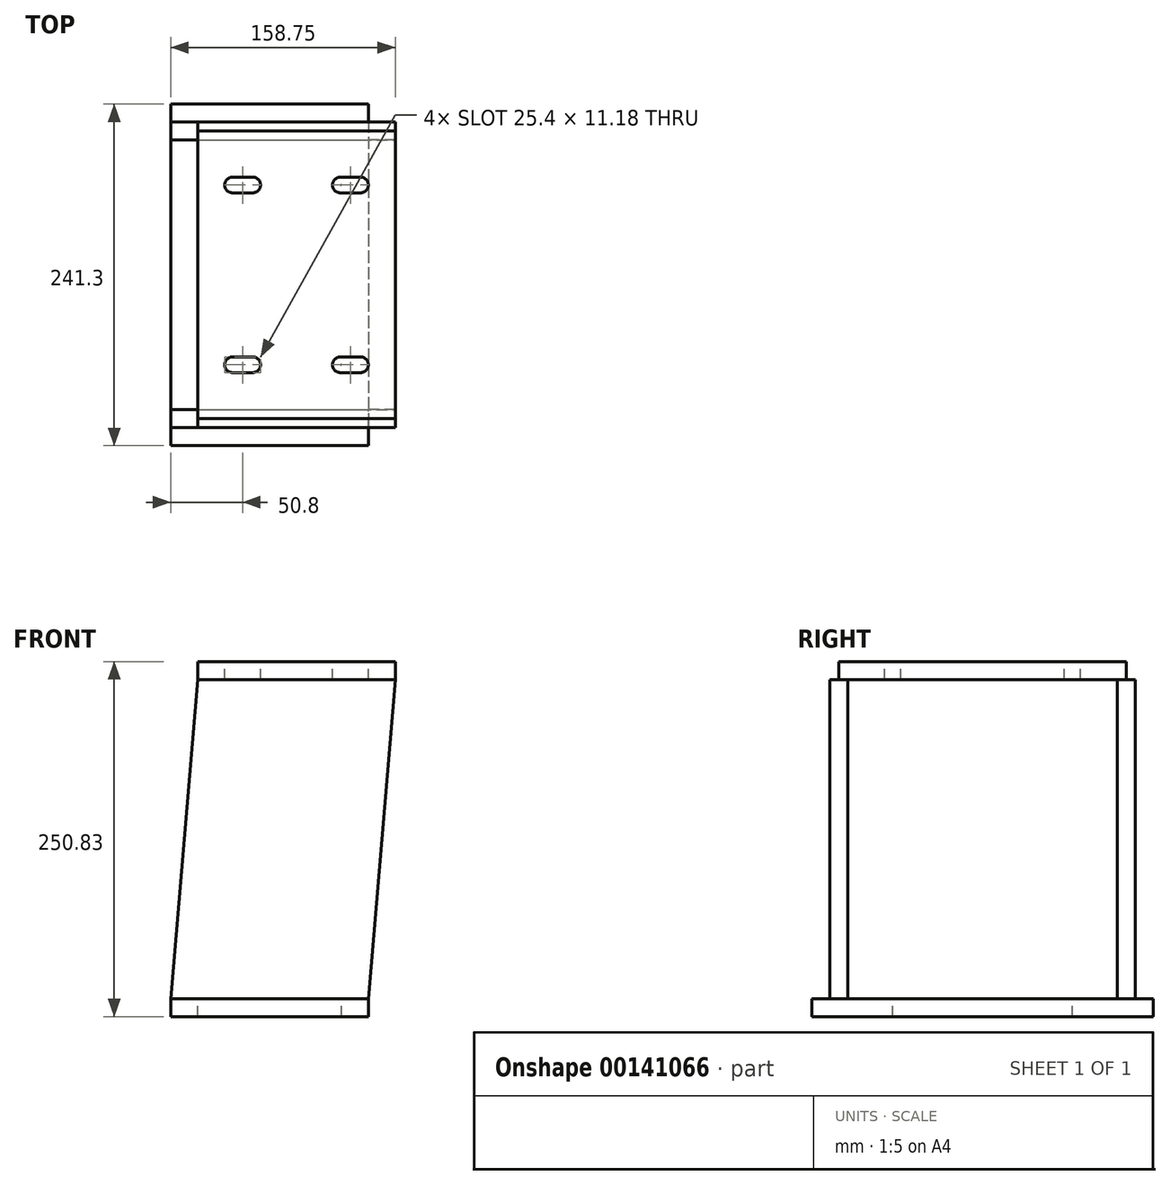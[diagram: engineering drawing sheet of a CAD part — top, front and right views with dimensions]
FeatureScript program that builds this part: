
annotation { "Feature Type Name" : "Feature", "Feature Type Description" : "" }
export const myFeature = defineFeature(function(context is Context, id is Id, definition is map)
    precondition{}
    {
        {
            var Q0;
            Q0=qCreatedBy(makeId("Top.planeOp"),FACE);
            cPlane(context, id + "F0", {"entities" : qUnion([Q0]), "cplaneType" : CPlaneType.OFFSET, "offset" : 250.82 * mm, "width" : 152.4 * mm, "height" : 152.4 * mm});
        }
        {
            var Q0;
            Q0=qCreatedBy(makeId("Top.planeOp"),FACE);
            var sketch = newSketch(context, id + "F1", { "sketchPlane" : qUnion([Q0])});
            skLineSegment(sketch, "E0.bottom", {"start": v(-69.85, 120.65) * mm, "end": v(69.85, 120.65) * mm});
            skLineSegment(sketch, "E0.top", {"start": v(-69.85, -120.65) * mm, "end": v(69.85, -120.65) * mm});
            skLineSegment(sketch, "E0.left", {"start": v(-69.85, 120.65) * mm, "end": v(-69.85, -120.65) * mm});
            skLineSegment(sketch, "E0.right", {"start": v(69.85, 120.65) * mm, "end": v(69.85, -120.65) * mm});
            skPoint(sketch, "E0.middle", {"position": v(0, 0) * mm});
            skSolve(sketch);
        }
        {
            var Q0;
            Q0 = qSketchRegion(id + "F1", true);
            extrude(context, id + "F2", {"entities" : qUnion([Q0]), "depth" : 12.7 * mm});
        }
        {
            var Q0;
            Q0=makeQuery(id+"F2.opExtrude","CAP_FACE",FACE,{"disambiguationData":[OSD([sQuery(id+"F1.wireOp",EDGE,"E0.bottom"),sQuery(id+"F1.wireOp",EDGE,"E0.top"),sQuery(id+"F1.wireOp",EDGE,"E0.left"),sQuery(id+"F1.wireOp",EDGE,"E0.right")])],"isStart":false});
            var sketch = newSketch(context, id + "F3", { "sketchPlane" : qUnion([Q0])});
            skLineSegment(sketch, "E1.0", {"start": v(69.85, 120.65) * mm, "end": v(69.85, -120.65) * mm, "construction": true});
            skLineSegment(sketch, "E2.0", {"start": v(50.8, 120.65) * mm, "end": v(50.8, -120.65) * mm, "construction": true});
            skLineSegment(sketch, "E3.0", {"start": v(-50.8, 120.65) * mm, "end": v(-50.8, -120.65) * mm, "construction": true});
            skLineSegment(sketch, "E4", {"start": v(-147.29, 0) * mm, "end": v(150.02, 0) * mm, "construction": true});
            skLineSegment(sketch, "E5.0", {"start": v(-147.29, -63.5) * mm, "end": v(150.02, -63.5) * mm, "construction": true});
            skLineSegment(sketch, "E6.MirrorCS", {"start": v(-147.29, 63.5) * mm, "end": v(150.02, 63.5) * mm, "construction": true});
            skPoint(sketch, "E7", {"position": v(-50.8, 63.5) * mm});
            skPoint(sketch, "E8", {"position": v(50.8, 63.5) * mm});
            skPoint(sketch, "E9", {"position": v(50.8, -63.5) * mm});
            skPoint(sketch, "E10", {"position": v(-50.8, -63.5) * mm});
            skSolve(sketch);
        }
        {
            var Q0;
            Q0=sQuery(id+"F3.wireOp",VERTEX,"E7");
            var Q1;
            Q1=sQuery(id+"F3.wireOp",VERTEX,"E8");
            var Q2;
            Q2=sQuery(id+"F3.wireOp",VERTEX,"E9");
            var Q3;
            Q3=sQuery(id+"F3.wireOp",VERTEX,"E10");
            var Q4;
            Q4=makeQuery(id+"F2.opExtrude","SWEPT_BODY",BODY,{"disambiguationData":[OSD([sQuery(id+"F1.wireOp",EDGE,"E0.bottom"),sQuery(id+"F1.wireOp",EDGE,"E0.top"),sQuery(id+"F1.wireOp",EDGE,"E0.left"),sQuery(id+"F1.wireOp",EDGE,"E0.right")])]});
            hole(context, id + "F4", {"style" : HoleStyle.SIMPLE, "endStyle" : HoleEndStyle.THROUGH, "standardTappedOrClearance" : lookupTablePath({ "standard" : "ANSI", "size" : "9/16 (0.56)", "type" : "Drilled" }), "standardBlindInLast" : lookupTablePath({ "standard" : "ANSI", "size" : "9/16", "type" : "Drilled" }), "holeDiameter" : 9 / 406.4 * mm, "locations" : qUnion([Q0, Q1, Q2, Q3]), "scope" : qUnion([Q4]), "isTappedThrough" : true});
        }
        {
            var Q0;
            Q0=qCreatedBy(id+"F0.planeOp",FACE);
            var sketch = newSketch(context, id + "F5", { "sketchPlane" : qUnion([Q0])});
            skLineSegment(sketch, "E11", {"start": v(0, 141.47) * mm, "end": v(0, -163.23) * mm, "construction": true});
            skLineSegment(sketch, "E12", {"start": v(-208.48, 0) * mm, "end": v(177.55, 0) * mm, "construction": true});
            skLineSegment(sketch, "E13.0", {"start": v(19.05, 141.47) * mm, "end": v(19.05, -163.23) * mm, "construction": true});
            skLineSegment(sketch, "E14.bottom", {"start": v(-50.8, 101.6) * mm, "end": v(88.9, 101.6) * mm});
            skLineSegment(sketch, "E14.top", {"start": v(-50.8, -101.6) * mm, "end": v(88.9, -101.6) * mm});
            skLineSegment(sketch, "E14.left", {"start": v(-50.8, 101.6) * mm, "end": v(-50.8, -101.6) * mm});
            skLineSegment(sketch, "E14.right", {"start": v(88.9, 101.6) * mm, "end": v(88.9, -101.6) * mm});
            skPoint(sketch, "E14.middle", {"position": v(19.05, 0) * mm});
            skSolve(sketch);
        }
        {
            var Q0;
            Q0 = qSketchRegion(id + "F5", true);
            extrude(context, id + "F6", {"entities" : qUnion([Q0]), "oppositeDirection" : true, "depth" : 12.7 * mm});
        }
        {
            var Q0;
            Q0=makeQuery(id+"F6.opExtrude","CAP_FACE",FACE,{"disambiguationData":[OSD([sQuery(id+"F5.wireOp",EDGE,"E14.bottom"),sQuery(id+"F5.wireOp",EDGE,"E14.top"),sQuery(id+"F5.wireOp",EDGE,"E14.left"),sQuery(id+"F5.wireOp",EDGE,"E14.right")])],"isStart":true});
            var sketch = newSketch(context, id + "F7", { "sketchPlane" : qUnion([Q0])});
            skLineSegment(sketch, "E15", {"start": v(-136.74, 0) * mm, "end": v(178.27, 0) * mm, "construction": true});
            skPoint(sketch, "E15.endSnap0", {"position": v(-50.8, 0) * mm});
            skLineSegment(sketch, "E16", {"start": v(19.05, 101.6) * mm, "end": v(19.05, -101.6) * mm, "construction": true});
            skLineSegment(sketch, "E17.0", {"start": v(-19.05, 101.6) * mm, "end": v(-19.05, -101.6) * mm, "construction": true});
            skLineSegment(sketch, "E18.0", {"start": v(-136.74, -63.5) * mm, "end": v(-26.16, -63.5) * mm, "construction": true});
            skLineSegment(sketch, "E19.0", {"start": v(-26.16, 101.6) * mm, "end": v(-26.16, -101.6) * mm, "construction": true});
            skLineSegment(sketch, "E20.MirrorCS", {"start": v(-11.94, 101.6) * mm, "end": v(-11.94, -101.6) * mm, "construction": true});
            skLineSegment(sketch, "E21.trimOffspring", {"start": v(-11.94, -63.5) * mm, "end": v(178.27, -63.5) * mm, "construction": true});
            skLineSegment(sketch, "E22", {"start": v(-26.16, -63.5) * mm, "end": v(-11.94, -63.5) * mm});
            skArc(sketch, "E23.0.startCap", {"start": v(-26.16, -69.09) * mm, "mid": v(-31.75, -63.5) * mm, "end": v(-26.16, -57.91) * mm});
            skArc(sketch, "E23.0.endCap", {"start": v(-11.94, -57.91) * mm, "mid": v(-6.35, -63.5) * mm, "end": v(-11.94, -69.09) * mm});
            skLineSegment(sketch, "E23.0.left", {"start": v(-26.16, -57.91) * mm, "end": v(-11.94, -57.91) * mm});
            skLineSegment(sketch, "E23.0.right", {"start": v(-26.16, -69.09) * mm, "end": v(-11.94, -69.09) * mm});
            skLineSegment(sketch, "E24.MirrorCS", {"start": v(64.26, -69.09) * mm, "end": v(50.04, -69.09) * mm});
            skLineSegment(sketch, "E25.MirrorCS", {"start": v(64.26, -57.91) * mm, "end": v(50.04, -57.91) * mm});
            skArc(sketch, "E26.MirrorCS", {"start": v(50.04, -57.91) * mm, "mid": v(44.45, -63.5) * mm, "end": v(50.04, -69.09) * mm});
            skArc(sketch, "E27.MirrorCS", {"start": v(64.26, -69.09) * mm, "mid": v(69.85, -63.5) * mm, "end": v(64.26, -57.91) * mm});
            skLineSegment(sketch, "E28.MirrorCS", {"start": v(64.26, -63.5) * mm, "end": v(50.04, -63.5) * mm});
            skLineSegment(sketch, "E29.MirrorCS", {"start": v(64.26, 69.09) * mm, "end": v(50.04, 69.09) * mm});
            skLineSegment(sketch, "E30.MirrorCS", {"start": v(-26.16, 69.09) * mm, "end": v(-11.94, 69.09) * mm});
            skLineSegment(sketch, "E31.MirrorCS", {"start": v(-26.16, 57.91) * mm, "end": v(-11.94, 57.91) * mm});
            skArc(sketch, "E32.MirrorCS", {"start": v(-11.94, 57.91) * mm, "mid": v(-6.35, 63.5) * mm, "end": v(-11.94, 69.09) * mm});
            skArc(sketch, "E33.MirrorCS", {"start": v(-26.16, 69.09) * mm, "mid": v(-31.75, 63.5) * mm, "end": v(-26.16, 57.91) * mm});
            skLineSegment(sketch, "E34.MirrorCS", {"start": v(-26.16, 63.5) * mm, "end": v(-11.94, 63.5) * mm});
            skLineSegment(sketch, "E35.MirrorCS", {"start": v(64.26, 63.5) * mm, "end": v(50.04, 63.5) * mm});
            skLineSegment(sketch, "E36.MirrorCS", {"start": v(64.26, 57.91) * mm, "end": v(50.04, 57.91) * mm});
            skArc(sketch, "E37.MirrorCS", {"start": v(50.04, 57.91) * mm, "mid": v(44.45, 63.5) * mm, "end": v(50.04, 69.09) * mm});
            skArc(sketch, "E38.MirrorCS", {"start": v(64.26, 69.09) * mm, "mid": v(69.85, 63.5) * mm, "end": v(64.26, 57.91) * mm});
            skSolve(sketch);
        }
        {
            var Q0;
            Q0 = qSketchRegion(id + "F7", true);
            extrude(context, id + "F8", {"entities" : qUnion([Q0]), "operationType" : NewBodyOperationType.REMOVE, "oppositeDirection" : true, "depth" : 25.4 * mm});
        }
        {
            var Q0;
            Q0=makeQuery(id+"F6.opExtrude","SWEPT_FACE",FACE,{"disambiguationData":[OSD([sQuery(id+"F5.wireOp",EDGE,"E14.top")])]});
            var sketch = newSketch(context, id + "F9", { "sketchPlane" : qUnion([Q0])});
            skLineSegment(sketch, "E39.0", {"start": v(-50.8, 238.13) * mm, "end": v(88.9, 238.13) * mm});
            skLineSegment(sketch, "E40.0", {"start": v(-69.85, 12.7) * mm, "end": v(69.85, 12.7) * mm});
            skLineSegment(sketch, "E41", {"start": v(-50.8, 238.13) * mm, "end": v(-69.85, 12.7) * mm});
            skLineSegment(sketch, "E42", {"start": v(88.9, 238.13) * mm, "end": v(69.85, 12.7) * mm});
            skSolve(sketch);
        }
        {
            var Q0;
            Q0 = qSketchRegion(id + "F9", true);
            extrude(context, id + "F10", {"entities" : qUnion([Q0]), "endBound" : BoundingType.SYMMETRIC, "depth" : 12.7 * mm});
        }
        {
            var Q0;
            Q0=makeQuery(id+"F10.opExtrude","SWEPT_BODY",BODY,{"disambiguationData":[OSD([sQuery(id+"F9.wireOp",EDGE,"E39.0"),sQuery(id+"F9.wireOp",EDGE,"E40.0"),sQuery(id+"F9.wireOp",EDGE,"E41"),sQuery(id+"F9.wireOp",EDGE,"E42")])]});
            var Q1;
            Q1=qCreatedBy(makeId("Front.planeOp"),FACE);
            mirror(context, id + "F11", {"entities" : qUnion([Q0]), "mirrorPlane" : qUnion([Q1])});
        }
    });
